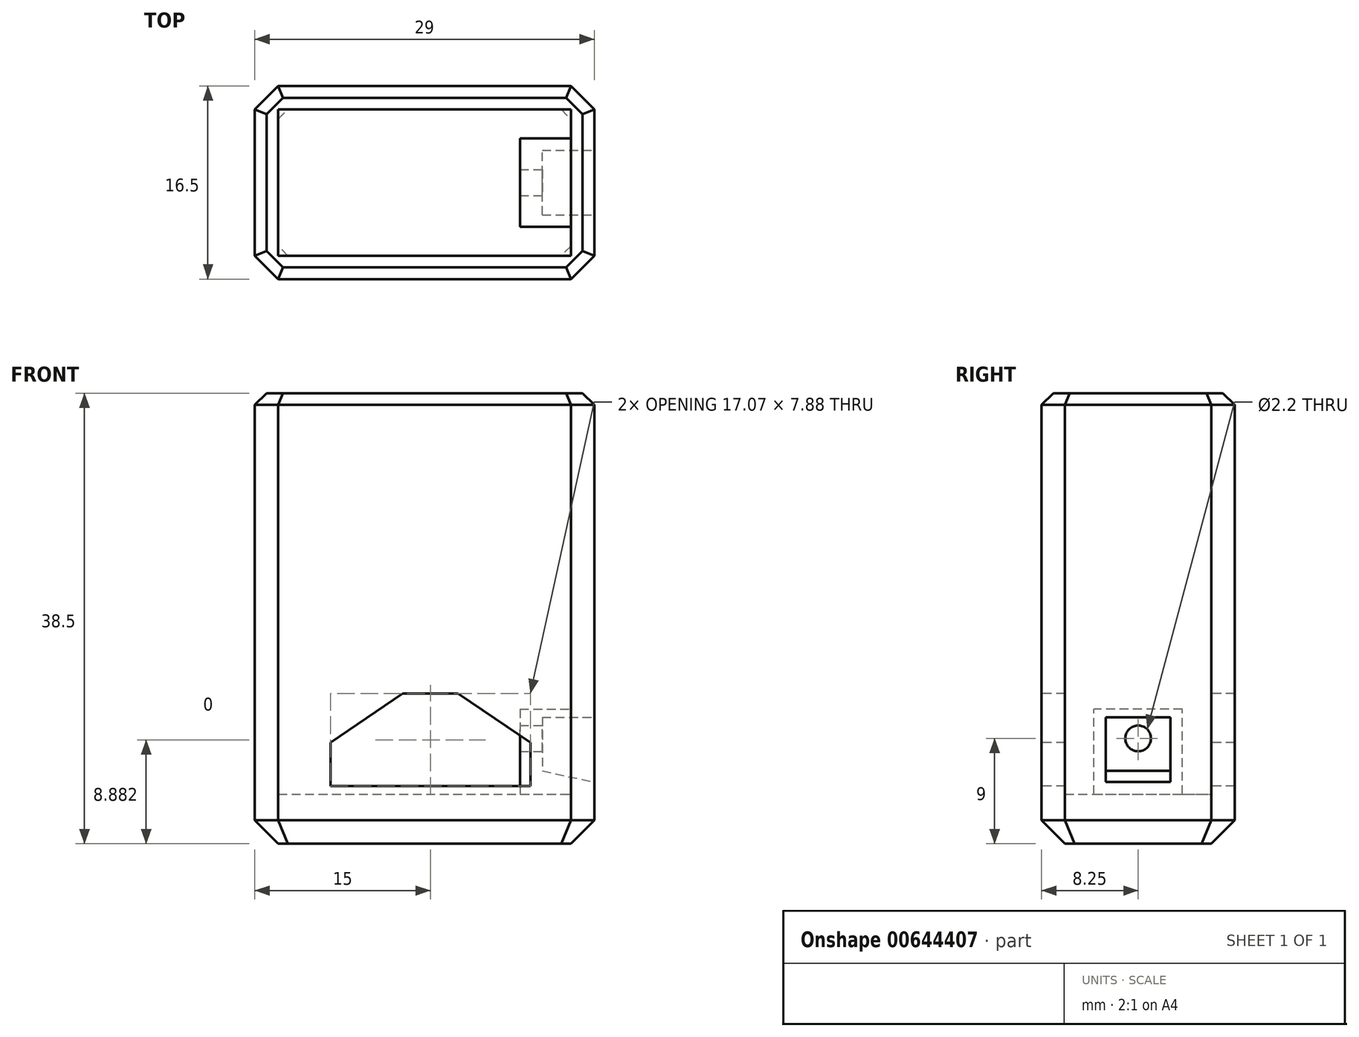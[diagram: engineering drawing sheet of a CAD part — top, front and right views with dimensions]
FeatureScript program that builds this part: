
annotation { "Feature Type Name" : "Feature", "Feature Type Description" : "" }
export const myFeature = defineFeature(function(context is Context, id is Id, definition is map)
    precondition{}
    {
        {
            var Q0;
            Q0=qCreatedBy(makeId("Top.planeOp"),FACE);
            var sketch = newSketch(context, id + "F0", { "sketchPlane" : qUnion([Q0])});
            skLineSegment(sketch, "E0.bottom", {"start": v(0, 0) * mm, "end": v(29, 0) * mm});
            skLineSegment(sketch, "E0.top", {"start": v(0, 16.5) * mm, "end": v(29, 16.5) * mm});
            skLineSegment(sketch, "E0.left", {"start": v(0, 0) * mm, "end": v(0, 16.5) * mm});
            skLineSegment(sketch, "E0.right", {"start": v(29, 0) * mm, "end": v(29, 16.5) * mm});
            skSolve(sketch);
        }
        {
            var Q0;
            Q0=makeQuery(id+"F0.imprint","IMPRINT",FACE,{"disambiguationData":[TD([[makeQuery(id+"F0.imprint","IMPRINT",EDGE,{"derivedFrom":sQuery(id+"F0.wireOp",EDGE,"E0.bottom")}),1.0]])]});
            extrude(context, id + "F1", {"entities" : qUnion([Q0]), "depth" : 38.5 * mm, "offsetDistance" : 25 * mm});
        }
        {
            var Q0;
            Q0=makeQuery(id+"F1.opExtrude","CAP_FACE",FACE,{"disambiguationData":[OSD([sQuery(id+"F0.wireOp",EDGE,"E0.bottom"),sQuery(id+"F0.wireOp",EDGE,"E0.top"),sQuery(id+"F0.wireOp",EDGE,"E0.left"),sQuery(id+"F0.wireOp",EDGE,"E0.right")])],"isStart":false});
            shell(context, id + "F2", {"entities" : qUnion([Q0]), "thickness" : 2 * mm});
        }
        {
            var Q0;
            Q0=makeQuery(id+"F2.opShell","OFFSET_FACE",FACE,{"disambiguationData":[OSD([sQuery(id+"F0.wireOp",EDGE,"E0.bottom"),sQuery(id+"F0.wireOp",EDGE,"E0.top"),sQuery(id+"F0.wireOp",EDGE,"E0.left"),sQuery(id+"F0.wireOp",EDGE,"E0.right")])]});
            extrude(context, id + "F3", {"entities" : qUnion([Q0]), "operationType" : NewBodyOperationType.ADD, "depth" : 2.25 * mm, "offsetDistance" : 25 * mm});
        }
        {
            var Q0;
            Q0=makeQuery(id+"F1.opExtrude","SWEPT_EDGE",EDGE,{"disambiguationData":[OSD([sQuery(id+"F0.wireOp",EDGE,"E0.bottom"),sQuery(id+"F0.wireOp",EDGE,"E0.right")])]});
            var Q1;
            Q1=makeQuery(id+"F1.opExtrude","SWEPT_EDGE",EDGE,{"disambiguationData":[OSD([sQuery(id+"F0.wireOp",EDGE,"E0.top"),sQuery(id+"F0.wireOp",EDGE,"E0.right")])]});
            var Q2;
            Q2=makeQuery(id+"F1.opExtrude","SWEPT_EDGE",EDGE,{"disambiguationData":[OSD([sQuery(id+"F0.wireOp",EDGE,"E0.top"),sQuery(id+"F0.wireOp",EDGE,"E0.left")])]});
            var Q3;
            Q3=makeQuery(id+"F1.opExtrude","SWEPT_EDGE",EDGE,{"disambiguationData":[OSD([sQuery(id+"F0.wireOp",EDGE,"E0.bottom"),sQuery(id+"F0.wireOp",EDGE,"E0.left")])]});
            chamfer(context, id + "F4", {"entities" : qUnion([Q0, Q1, Q2, Q3]), "width" : 2 * mm, "tangentPropagation" : true});
        }
        {
            var Q0;
            Q0=makeQuery(id+"F1.opExtrude","CAP_FACE",FACE,{"disambiguationData":[OSD([sQuery(id+"F0.wireOp",EDGE,"E0.bottom"),sQuery(id+"F0.wireOp",EDGE,"E0.top"),sQuery(id+"F0.wireOp",EDGE,"E0.left"),sQuery(id+"F0.wireOp",EDGE,"E0.right")])],"isStart":true});
            chamfer(context, id + "F5", {"entities" : qUnion([Q0]), "width" : 2 * mm, "tangentPropagation" : true});
        }
        {
            var Q0;
            Q0=makeQuery(id+"F1.opExtrude","CAP_EDGE",EDGE,{"disambiguationData":[OSD([sQuery(id+"F0.wireOp",EDGE,"E0.left")])],"isStart":false});
            var Q1;
            {var subQ0=sQuery(id+"F0.wireOp",EDGE,"E0.left");var subQ1=sQuery(id+"F0.wireOp",EDGE,"E0.bottom");Q1=makeQuery(id+"F4.opChamfer","BLEND_EDGE",EDGE,{"blendedFrom":[makeQuery(id+"F1.opExtrude","SWEPT_EDGE",EDGE,{"disambiguationData":[OSD([subQ1,subQ0])]}),makeQuery(id+"F1.opExtrude","CAP_FACE",FACE,{"disambiguationData":[OSD([subQ1,sQuery(id+"F0.wireOp",EDGE,"E0.top"),subQ0,sQuery(id+"F0.wireOp",EDGE,"E0.right")])],"isStart":false})],"blendedInto":[makeQuery(id+"F1.opExtrude","CAP_FACE",FACE,{"disambiguationData":[OSD([subQ1,sQuery(id+"F0.wireOp",EDGE,"E0.top"),subQ0,sQuery(id+"F0.wireOp",EDGE,"E0.right")])],"isStart":false})]});}
            var Q2;
            Q2=makeQuery(id+"F1.opExtrude","CAP_EDGE",EDGE,{"disambiguationData":[OSD([sQuery(id+"F0.wireOp",EDGE,"E0.bottom")])],"isStart":false});
            var Q3;
            {var subQ0=sQuery(id+"F0.wireOp",EDGE,"E0.right");var subQ1=sQuery(id+"F0.wireOp",EDGE,"E0.bottom");Q3=makeQuery(id+"F4.opChamfer","BLEND_EDGE",EDGE,{"blendedFrom":[makeQuery(id+"F1.opExtrude","SWEPT_EDGE",EDGE,{"disambiguationData":[OSD([subQ1,subQ0])]}),makeQuery(id+"F1.opExtrude","CAP_FACE",FACE,{"disambiguationData":[OSD([subQ1,sQuery(id+"F0.wireOp",EDGE,"E0.top"),sQuery(id+"F0.wireOp",EDGE,"E0.left"),subQ0])],"isStart":false})],"blendedInto":[makeQuery(id+"F1.opExtrude","CAP_FACE",FACE,{"disambiguationData":[OSD([subQ1,sQuery(id+"F0.wireOp",EDGE,"E0.top"),sQuery(id+"F0.wireOp",EDGE,"E0.left"),subQ0])],"isStart":false})]});}
            var Q4;
            Q4=makeQuery(id+"F1.opExtrude","CAP_EDGE",EDGE,{"disambiguationData":[OSD([sQuery(id+"F0.wireOp",EDGE,"E0.right")])],"isStart":false});
            var Q5;
            {var subQ0=sQuery(id+"F0.wireOp",EDGE,"E0.right");var subQ1=sQuery(id+"F0.wireOp",EDGE,"E0.top");Q5=makeQuery(id+"F4.opChamfer","BLEND_EDGE",EDGE,{"blendedFrom":[makeQuery(id+"F1.opExtrude","SWEPT_EDGE",EDGE,{"disambiguationData":[OSD([subQ1,subQ0])]}),makeQuery(id+"F1.opExtrude","CAP_FACE",FACE,{"disambiguationData":[OSD([sQuery(id+"F0.wireOp",EDGE,"E0.bottom"),subQ1,sQuery(id+"F0.wireOp",EDGE,"E0.left"),subQ0])],"isStart":false})],"blendedInto":[makeQuery(id+"F1.opExtrude","CAP_FACE",FACE,{"disambiguationData":[OSD([sQuery(id+"F0.wireOp",EDGE,"E0.bottom"),subQ1,sQuery(id+"F0.wireOp",EDGE,"E0.left"),subQ0])],"isStart":false})]});}
            var Q6;
            Q6=makeQuery(id+"F1.opExtrude","CAP_EDGE",EDGE,{"disambiguationData":[OSD([sQuery(id+"F0.wireOp",EDGE,"E0.top")])],"isStart":false});
            var Q7;
            {var subQ0=sQuery(id+"F0.wireOp",EDGE,"E0.left");var subQ1=sQuery(id+"F0.wireOp",EDGE,"E0.top");Q7=makeQuery(id+"F4.opChamfer","BLEND_EDGE",EDGE,{"blendedFrom":[makeQuery(id+"F1.opExtrude","SWEPT_EDGE",EDGE,{"disambiguationData":[OSD([subQ1,subQ0])]}),makeQuery(id+"F1.opExtrude","CAP_FACE",FACE,{"disambiguationData":[OSD([sQuery(id+"F0.wireOp",EDGE,"E0.bottom"),subQ1,subQ0,sQuery(id+"F0.wireOp",EDGE,"E0.right")])],"isStart":false})],"blendedInto":[makeQuery(id+"F1.opExtrude","CAP_FACE",FACE,{"disambiguationData":[OSD([sQuery(id+"F0.wireOp",EDGE,"E0.bottom"),subQ1,subQ0,sQuery(id+"F0.wireOp",EDGE,"E0.right")])],"isStart":false})]});}
            chamfer(context, id + "F6", {"entities" : qUnion([Q0, Q1, Q2, Q3, Q4, Q5, Q6, Q7]), "width" : 1 * mm, "tangentPropagation" : true});
        }
        {
            var Q0;
            Q0=makeQuery(id+"F1.opExtrude","SWEPT_FACE",FACE,{"disambiguationData":[OSD([sQuery(id+"F0.wireOp",EDGE,"E0.bottom")])]});
            var sketch = newSketch(context, id + "F7", { "sketchPlane" : qUnion([Q0])});
            skLineSegment(sketch, "E1", {"start": v(17.36, 12.82) * mm, "end": v(12.63, 12.82) * mm});
            skLineSegment(sketch, "E2", {"start": v(12.63, 12.82) * mm, "end": v(6.46, 8.66) * mm});
            skLineSegment(sketch, "E3", {"start": v(6.46, 8.66) * mm, "end": v(6.46, 4.94) * mm});
            skLineSegment(sketch, "E4", {"start": v(6.46, 4.94) * mm, "end": v(23.54, 4.94) * mm});
            skLineSegment(sketch, "E5", {"start": v(23.54, 4.94) * mm, "end": v(23.54, 8.66) * mm});
            skLineSegment(sketch, "E6", {"start": v(23.54, 8.66) * mm, "end": v(17.36, 12.82) * mm});
            skSolve(sketch);
        }
        {
            var Q0;
            Q0=makeQuery(id+"F7.imprint","IMPRINT",FACE,{"disambiguationData":[TD([[makeQuery(id+"F7.imprint","IMPRINT",EDGE,{"derivedFrom":sQuery(id+"F7.wireOp",EDGE,"E1")}),1.0]])]});
            extrude(context, id + "F8", {"entities" : qUnion([Q0]), "operationType" : NewBodyOperationType.REMOVE, "endBound" : BoundingType.THROUGH_ALL, "oppositeDirection" : true, "depth" : 25 * mm, "offsetDistance" : 25 * mm});
        }
        {
            var Q0;
            Q0=makeQuery(id+"F1.opExtrude","SWEPT_FACE",FACE,{"disambiguationData":[OSD([sQuery(id+"F0.wireOp",EDGE,"E0.right")])]});
            var sketch = newSketch(context, id + "F9", { "sketchPlane" : qUnion([Q0])});
            skLineSegment(sketch, "E7.bottom", {"start": v(4.48, 11.5) * mm, "end": v(12.02, 11.5) * mm});
            skLineSegment(sketch, "E7.top", {"start": v(4.48, 4.25) * mm, "end": v(12.02, 4.25) * mm});
            skLineSegment(sketch, "E7.left", {"start": v(4.48, 11.5) * mm, "end": v(4.48, 4.25) * mm});
            skLineSegment(sketch, "E7.right", {"start": v(12.02, 11.5) * mm, "end": v(12.02, 4.25) * mm});
            skCircle(sketch, "E8", {"center": v(8.25, 9) * mm, "radius": 1.1 * mm});
            skSolve(sketch);
        }
        {
            var Q0;
            Q0=makeQuery(id+"F9.imprint","IMPRINT",FACE,{"disambiguationData":[TD([[makeQuery(id+"F9.imprint","IMPRINT",EDGE,{"derivedFrom":sQuery(id+"F9.wireOp",EDGE,"E7.bottom")}),-1.0]])]});
            extrude(context, id + "F10", {"entities" : qUnion([Q0]), "operationType" : NewBodyOperationType.ADD, "oppositeDirection" : true, "depth" : 6.35 * mm, "offsetDistance" : 25 * mm});
        }
        {
            var Q0;
            Q0=makeQuery(id+"F1.opExtrude","SWEPT_FACE",FACE,{"disambiguationData":[OSD([sQuery(id+"F0.wireOp",EDGE,"E0.right")])]});
            var sketch = newSketch(context, id + "F11", { "sketchPlane" : qUnion([Q0])});
            skLineSegment(sketch, "E9.bottom", {"start": v(5.48, 10.8) * mm, "end": v(11.02, 10.8) * mm});
            skLineSegment(sketch, "E9.top", {"start": v(5.48, 5.27) * mm, "end": v(11.02, 5.27) * mm});
            skLineSegment(sketch, "E9.left", {"start": v(5.48, 10.8) * mm, "end": v(5.48, 5.27) * mm});
            skLineSegment(sketch, "E9.right", {"start": v(11.02, 10.8) * mm, "end": v(11.02, 5.27) * mm});
            skSolve(sketch);
        }
        {
            var Q0;
            Q0=makeQuery(id+"F11.imprint","IMPRINT",FACE,{"disambiguationData":[TD([[makeQuery(id+"F11.imprint","IMPRINT",EDGE,{"derivedFrom":sQuery(id+"F11.wireOp",EDGE,"E9.bottom")}),-1.0]])]});
            cPlane(context, id + "F12", {"entities" : qUnion([Q0]), "cplaneType" : CPlaneType.OFFSET, "offset" : 4.45 * mm, "oppositeDirection" : true, "width" : 150 * mm, "height" : 150 * mm});
        }
        {
            var Q0;
            Q0=qCreatedBy(id+"F12.planeOp",FACE);
            var sketch = newSketch(context, id + "F13", { "sketchPlane" : qUnion([Q0])});
            skLineSegment(sketch, "E10.bottom", {"start": v(5.48, 10.8) * mm, "end": v(11.02, 10.8) * mm});
            skLineSegment(sketch, "E10.top", {"start": v(5.48, 6.22) * mm, "end": v(11.02, 6.22) * mm});
            skLineSegment(sketch, "E10.left", {"start": v(5.48, 10.8) * mm, "end": v(5.48, 6.22) * mm});
            skLineSegment(sketch, "E10.right", {"start": v(11.02, 10.8) * mm, "end": v(11.02, 6.22) * mm});
            skSolve(sketch);
        }
        {
            var Q1;
            Q1 = qSketchRegion(id + "F13", true);
            var Q2;
            Q2 = qSketchRegion(id + "F11", true);
            loft(context, id + "F14", {"operationType" : NewBodyOperationType.REMOVE, "sheetProfilesArray" : [{ "sheetProfileEntities" : qUnion([Q1]) }, { "sheetProfileEntities" : qUnion([Q2]) }]});
        }
    });
